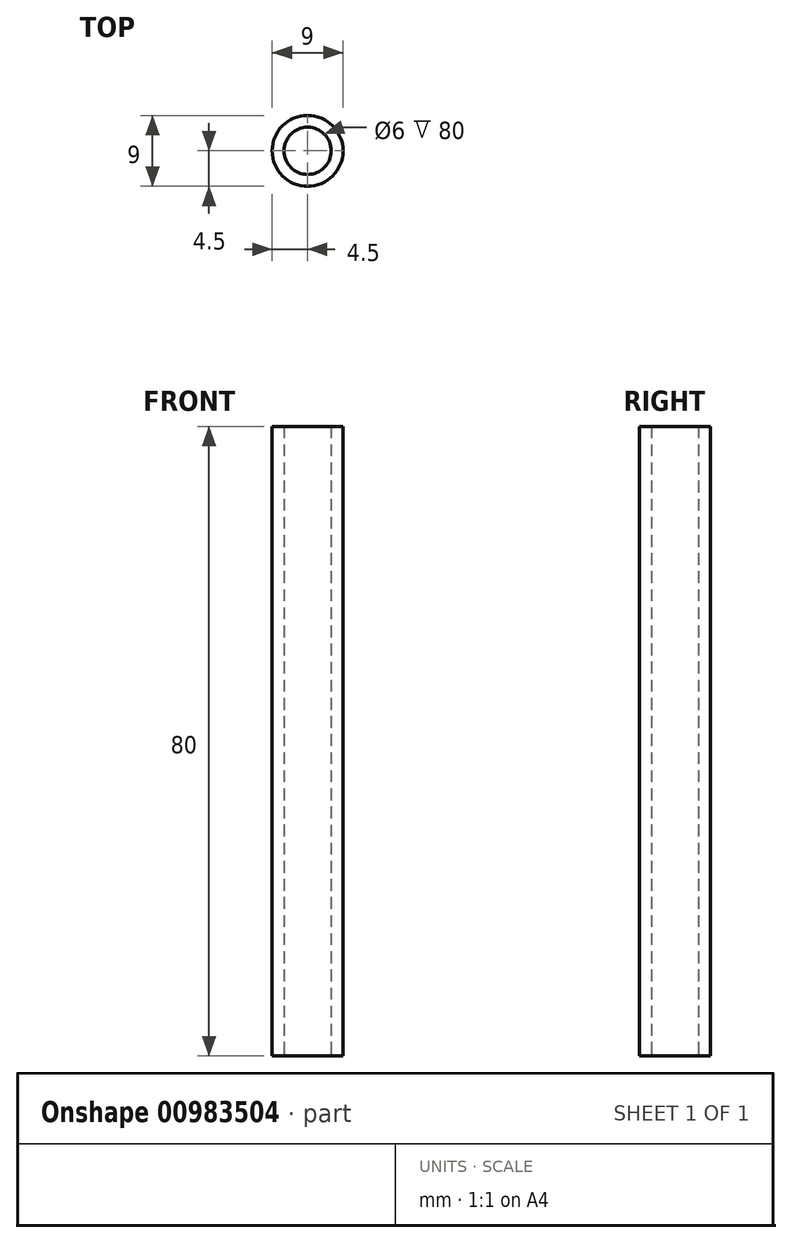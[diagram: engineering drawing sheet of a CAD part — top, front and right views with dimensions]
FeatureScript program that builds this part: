
annotation { "Feature Type Name" : "Feature", "Feature Type Description" : "" }
export const myFeature = defineFeature(function(context is Context, id is Id, definition is map)
    precondition{}
    {
        {
            var Q0;
            Q0=qCreatedBy(makeId("Top.planeOp"),FACE);
            var sketch = newSketch(context, id + "F0", { "sketchPlane" : qUnion([Q0])});
            skCircle(sketch, "E0", {"center": v(0, 0) * mm, "radius": 3 * mm});
            skCircle(sketch, "E1.0", {"center": v(0, 0) * mm, "radius": 4.5 * mm});
            skSolve(sketch);
        }
        {
            var Q0;
            Q0=makeQuery(id+"F0.imprint","IMPRINT",FACE,{"disambiguationData":[TD([[makeQuery(id+"F0.imprint","IMPRINT",EDGE,{"derivedFrom":sQuery(id+"F0.wireOp",EDGE,"E0")}),-1.0]])]});
            extrude(context, id + "F1", {"entities" : qUnion([Q0]), "depth" : 80 * mm, "offsetDistance" : 25 * mm});
        }
    });
